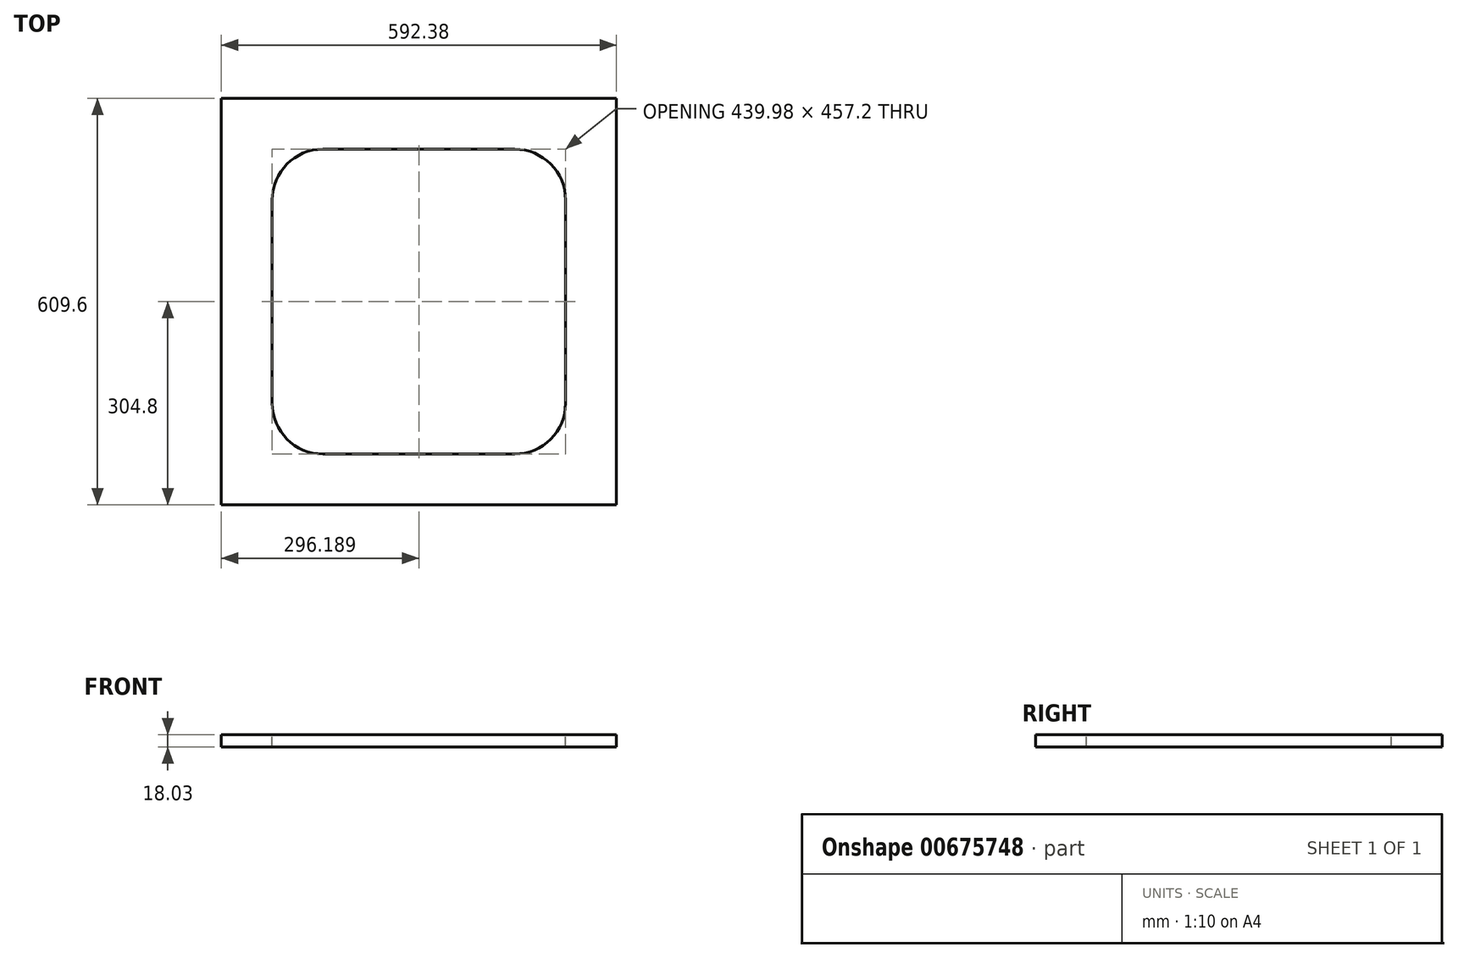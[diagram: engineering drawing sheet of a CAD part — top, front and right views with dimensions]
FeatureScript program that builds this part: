
annotation { "Feature Type Name" : "Feature", "Feature Type Description" : "" }
export const myFeature = defineFeature(function(context is Context, id is Id, definition is map)
    precondition{}
    {
        {
            var Q0;
            Q0=qCreatedBy(makeId("Top.planeOp"),FACE);
            var sketch = newSketch(context, id + "F0", { "sketchPlane" : qUnion([Q0])});
            skLineSegment(sketch, "E0.bottom", {"start": v(0, 0) * mm, "end": v(592.38, 0) * mm});
            skLineSegment(sketch, "E0.top", {"start": v(0, 609.6) * mm, "end": v(592.38, 609.6) * mm});
            skLineSegment(sketch, "E0.left", {"start": v(0, 0) * mm, "end": v(0, 609.6) * mm});
            skLineSegment(sketch, "E0.right", {"start": v(592.38, 0) * mm, "end": v(592.38, 609.6) * mm});
            skSolve(sketch);
        }
        {
            var Q0;
            Q0 = qSketchRegion(id + "F0", true);
            extrude(context, id + "F1", {"entities" : qUnion([Q0]), "depth" : 18.03 * mm, "offsetDistance" : 25.4 * mm});
        }
        {
            var Q0;
            Q0=makeQuery(id+"F1.opExtrude","CAP_FACE",FACE,{"disambiguationData":[OSD([sQuery(id+"F0.wireOp",EDGE,"E0.bottom"),sQuery(id+"F0.wireOp",EDGE,"E0.top"),sQuery(id+"F0.wireOp",EDGE,"E0.left"),sQuery(id+"F0.wireOp",EDGE,"E0.right")])],"isStart":false});
            var sketch = newSketch(context, id + "F2", { "sketchPlane" : qUnion([Q0])});
            skLineSegment(sketch, "E1.0", {"start": v(76.2, 533.4) * mm, "end": v(516.18, 533.4) * mm});
            skLineSegment(sketch, "E1.1", {"start": v(76.2, 76.2) * mm, "end": v(76.2, 533.4) * mm});
            skLineSegment(sketch, "E1.2", {"start": v(76.2, 76.2) * mm, "end": v(516.18, 76.2) * mm});
            skLineSegment(sketch, "E1.3", {"start": v(516.18, 76.2) * mm, "end": v(516.18, 533.4) * mm});
            skSolve(sketch);
        }
        {
            var Q0;
            Q0 = qSketchRegion(id + "F2", true);
            extrude(context, id + "F3", {"entities" : qUnion([Q0]), "operationType" : NewBodyOperationType.REMOVE, "endBound" : BoundingType.THROUGH_ALL, "oppositeDirection" : true, "depth" : 25.4 * mm, "offsetDistance" : 25.4 * mm});
        }
        {
            var Q0;
            Q0=makeQuery(id+"F3.boolean.opBoolean","COPY",EDGE,{"derivedFrom":makeQuery(id+"F3.opExtrude","SWEPT_EDGE",EDGE,{"disambiguationData":[OSD([sQuery(id+"F2.wireOp",EDGE,"E1.0"),sQuery(id+"F2.wireOp",EDGE,"E1.3")])]})});
            var Q1;
            Q1=makeQuery(id+"F3.boolean.opBoolean","COPY",EDGE,{"derivedFrom":makeQuery(id+"F3.opExtrude","SWEPT_EDGE",EDGE,{"disambiguationData":[OSD([sQuery(id+"F2.wireOp",EDGE,"E1.0"),sQuery(id+"F2.wireOp",EDGE,"E1.1")])]})});
            var Q2;
            Q2=makeQuery(id+"F3.boolean.opBoolean","COPY",EDGE,{"derivedFrom":makeQuery(id+"F3.opExtrude","SWEPT_EDGE",EDGE,{"disambiguationData":[OSD([sQuery(id+"F2.wireOp",EDGE,"E1.1"),sQuery(id+"F2.wireOp",EDGE,"E1.2")])]})});
            var Q3;
            Q3=makeQuery(id+"F3.boolean.opBoolean","COPY",EDGE,{"derivedFrom":makeQuery(id+"F3.opExtrude","SWEPT_EDGE",EDGE,{"disambiguationData":[OSD([sQuery(id+"F2.wireOp",EDGE,"E1.2"),sQuery(id+"F2.wireOp",EDGE,"E1.3")])]})});
            fillet(context, id + "F4", {"entities" : qUnion([Q0, Q1, Q2, Q3]), "radius" : 76.2 * mm, "tangentPropagation" : true, "allowEdgeOverflow" : false});
        }
    });
